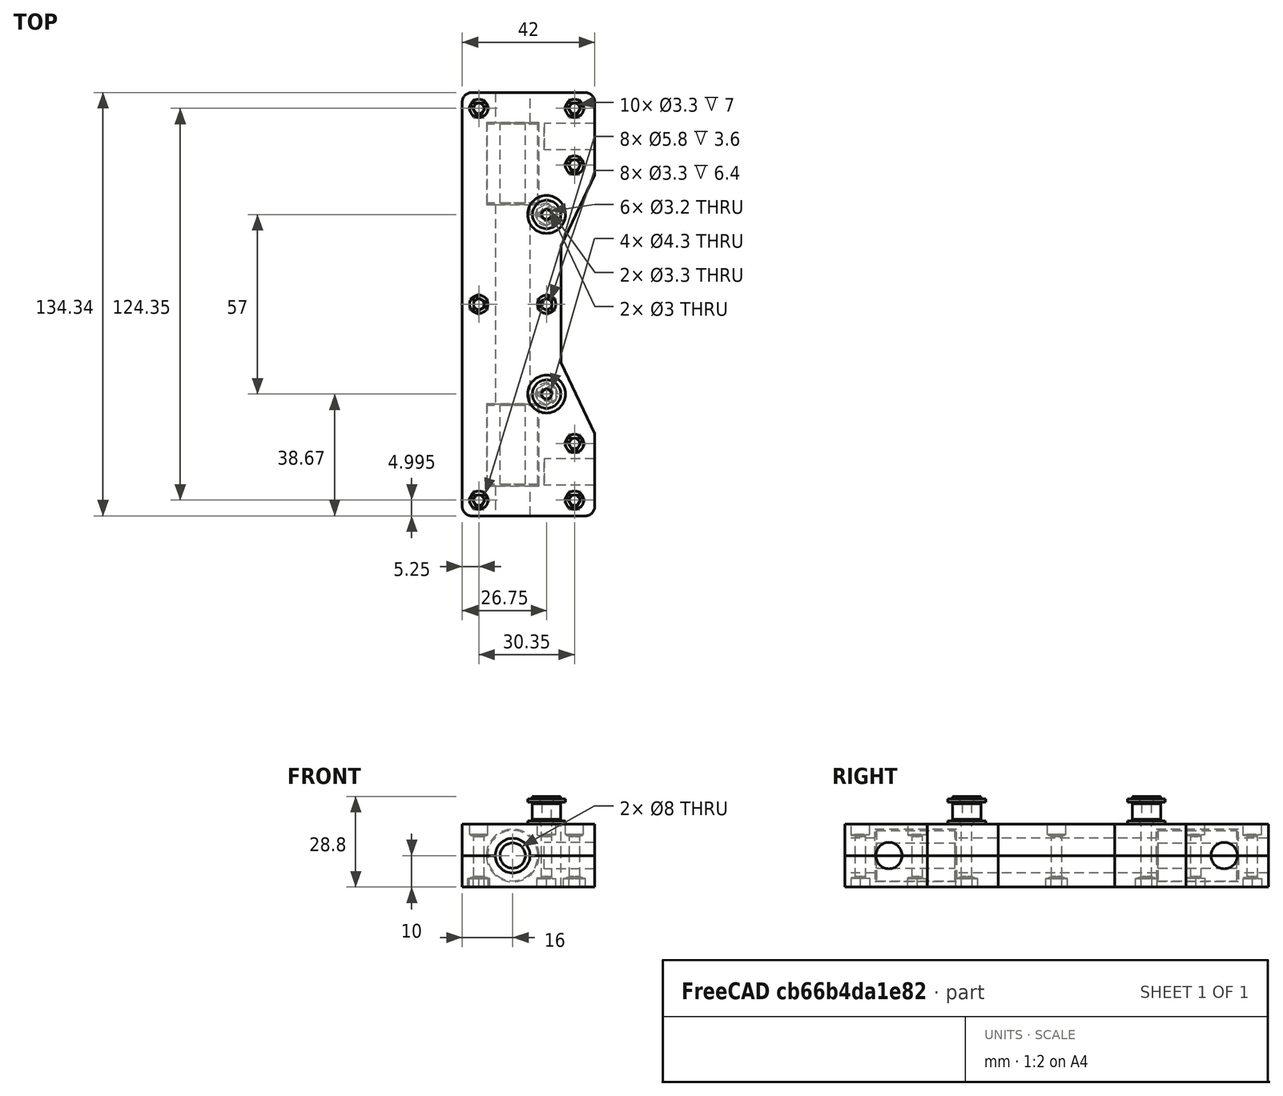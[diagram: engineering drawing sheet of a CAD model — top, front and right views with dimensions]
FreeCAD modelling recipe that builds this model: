
FCSTD DOCUMENT  (FreeCAD 0.16R6706 (Git))
Label: endshaftslid_rodsep_106_35_pullsep_57
License: All rights reserved
LicenseURL: http://en.wikipedia.org/wiki/All_rights_reserved
objects: Part::FeaturePython×11, Part::Prism×10, Part::Cylinder×6, Part::Feature×6, Part::Extrusion×5, Part::Circle×4, Part::MultiFuse×4, Part::Cut×3, Part::Common×3, Part::Box×2, Part::Fillet×2, Part::Compound×2, Part::Polygon×1, Part::Fuse×1
note: 60 computed .brp shape members not serialized (recipe doc carries the construction recipe); baked Part::Feature solids carry a one-line shape summary decoded from their .brp

FEATURE [Part::Box] topsideslid_box
  Height = 10
  Length = 42
  Placement = pos=(-16,-67.175,0) rot=(0,0,1;0rad)
  Width = 134.35
FEATURE [Part::Box] bosidetslid_box
  Height = 10
  Length = 42
  Placement = pos=(-16,-67.175,-10) rot=(0,0,1;0rad)
  Width = 134.35
FEATURE [Part::Fillet] topsideslid_fllt
  Base = -> topsideslid_box
  Edges = 4 edges r=3: [Edge1,Edge3,Edge5,Edge7]
FEATURE [Part::Fillet] botsideslid_fllt
  Base = -> bosidetslid_box
  Edges = 4 edges r=3: [Edge1,Edge3,Edge5,Edge7]
FEATURE [Part::Circle] sliderod_circ
  Angle0 = 0
  Angle1 = 360
  Placement = pos=(0,-68.175,0) rot=(-1,0,0;1.5708rad)
  Radius = 5.5
FEATURE [Part::Extrusion] sliderod
  Base = -> sliderod_circ
  Dir = (0,136.35,0)
  Solid = true
FEATURE [Part::Cylinder] lm8uu_0_ext
  Angle = 360
  Height = 25
  Placement = pos=(0,-57.175,0) rot=(-1,0,0;1.5708rad)
  Radius = 8
FEATURE [Part::Cylinder] lm8uu_0_int
  Angle = 360
  Height = 27
  Placement = pos=(0,-58.175,0) rot=(-1,0,0;1.5708rad)
  Radius = 4
FEATURE [Part::Cut] lm8uu_0
  Base = -> lm8uu_0_ext
  Tool = -> lm8uu_0_int
FEATURE [Part::Circle] lm8uu_0_cont_circ
  Angle0 = 0
  Angle1 = 360
  Placement = pos=(0,-57.675,0) rot=(-1,0,0;1.5708rad)
  Radius = 8.35
FEATURE [Part::Extrusion] lm8uu_0_cont
  Base = -> lm8uu_0_cont_circ
  Dir = (0,26,0)
  Solid = true
FEATURE [Part::FeaturePython] Clone  label="lm8uu_1"  # Draft clone (typed FeaturePython)
  Objects = -> [lm8uu_0]
  Placement = pos=(0,89.35,0) rot=(0,0,1;0rad)
  Scale = (1,1,1)
FEATURE [Part::FeaturePython] Clone001  label="lm8uu_1_cont"  # Draft clone (typed FeaturePython)
  Objects = -> [lm8uu_0_cont]
  Placement = pos=(0,89.35,0) rot=(0,0,1;0rad)
  Scale = (1,1,1)
FEATURE [Part::Circle] holdrod_0_circ
  Angle0 = 0
  Angle1 = 360
  Placement = pos=(10,0,0) rot=(0,1,0;1.5708rad)
  Radius = 4.175
FEATURE [Part::Extrusion] holdrod_0
  Base = -> holdrod_0_circ
  Dir = (17,0,0)
  Placement = pos=(0,-53.175,0) rot=(0,0,1;0rad)
  Solid = true
FEATURE [Part::Circle] holdrod_1_circ
  Angle0 = 0
  Angle1 = 360
  Placement = pos=(10,0,0) rot=(0,1,0;1.5708rad)
  Radius = 4.175
FEATURE [Part::Extrusion] holdrod_1
  Base = -> holdrod_1_circ
  Dir = (17,0,0)
  Placement = pos=(0,53.175,0) rot=(0,0,1;0rad)
  Solid = true
FEATURE [Part::Cylinder] bolt_hole_bolt_shank
  Angle = 360
  Height = 22
  Placement = pos=(0,0,-1) rot=(0,0,1;0rad)
  Radius = 1.65
FEATURE [Part::Cylinder] bolt_hole_bolt_head
  Angle = 360
  Height = 4.3
  Placement = pos=(0,0,16.7) rot=(0,0,1;0rad)
  Radius = 2.9
FEATURE [Part::Prism] bolt_hole_bolt_sup1
  Circumradius = 3.3
  Height = 3.6
  Placement = pos=(0,0,16.4) rot=(0,0,1;0.523599rad)
  Polygon = 3
FEATURE [Part::Cylinder] bolt_hole_bolt_sup1away
  Angle = 360
  Height = 3.6
  Placement = pos=(0,0,16.4) rot=(0,0,1;0rad)
  Radius = 2.9
FEATURE [Part::Common] sup1cut
  Base = -> bolt_hole_bolt_sup1
  Tool = -> bolt_hole_bolt_sup1away
FEATURE [Part::Prism] bolt_hole_bolt_sup2
  Circumradius = 1.8975
  Height = 3.9
  Placement = pos=(0,0,16.1) rot=(0,0,1;0rad)
  Polygon = 6
FEATURE [Part::MultiFuse] bolt_hole_bolt
  Shapes = -> [bolt_hole_bolt_shank,bolt_hole_bolt_head,sup1cut,bolt_hole_bolt_sup2]
FEATURE [Part::Prism] bolt_hole_nut
  Circumradius = 3.455
  Height = 3.7
  Placement = pos=(0,0,-1) rot=(0,0,1;0rad)
  Polygon = 6
FEATURE [Part::Prism] bolt_hole_nutsup1
  Circumradius = 3.3
  Height = 3
  Placement = pos=(0,0,0) rot=(0,0,1;0.523599rad)
  Polygon = 3
FEATURE [Part::Prism] bolt_hole_supnut1away
  Circumradius = 3.455
  Height = 3
  Polygon = 6
FEATURE [Part::Common] supnut1_cut
  Base = -> bolt_hole_nutsup1
  Tool = -> bolt_hole_supnut1away
FEATURE [Part::Prism] bolt_hole_supnut2
  Circumradius = 1.8975
  Height = 3.3
  Polygon = 6
FEATURE [Part::MultiFuse] boltnut
  Placement = pos=(-10.75,0,-10) rot=(0,0,1;1.5708rad)
  Shapes = -> [bolt_hole_bolt,bolt_hole_nut,supnut1_cut,bolt_hole_supnut2]
FEATURE [Part::FeaturePython] Clone002  label="bolt_hole_r"  # Draft clone (typed FeaturePython)
  Objects = -> [boltnut]
  Placement = pos=(10.75,0,-10) rot=(0,0,1;0.523599rad)
  Scale = (1,1,1)
FEATURE [Part::FeaturePython] Clone003  label="bolt_hole_lu"  # Draft clone (typed FeaturePython)
  Objects = -> [boltnut]
  Placement = pos=(-10.75,-62.175,-10) rot=(0,0,1;0rad)
  Scale = (1,1,1)
FEATURE [Part::FeaturePython] Clone004  label="bolt_hole_ld"  # Draft clone (typed FeaturePython)
  Objects = -> [boltnut]
  Placement = pos=(-10.75,62.175,-10) rot=(0,0,1;0rad)
  Scale = (1,1,1)
FEATURE [Part::FeaturePython] Clone005  label="bolt_hole_ru"  # Draft clone (typed FeaturePython)
  Objects = -> [boltnut]
  Placement = pos=(19.6,62.175,-10) rot=(0,0,1;0rad)
  Scale = (1,1,1)
FEATURE [Part::FeaturePython] Clone006  label="bolt_hole_rd"  # Draft clone (typed FeaturePython)
  Objects = -> [boltnut]
  Placement = pos=(19.6,-62.175,-10) rot=(0,0,1;0rad)
  Scale = (1,1,1)
FEATURE [Part::FeaturePython] Clone007  label="bolt_hole_rmu"  # Draft clone (typed FeaturePython)
  Objects = -> [boltnut]
  Placement = pos=(19.6,44.175,-10) rot=(0,0,1;0rad)
  Scale = (1,1,1)
FEATURE [Part::FeaturePython] Clone008  label="bolt_hole_rmd"  # Draft clone (typed FeaturePython)
  Objects = -> [boltnut]
  Placement = pos=(19.6,-44.175,-10) rot=(0,0,1;0rad)
  Scale = (1,1,1)
FEATURE [Part::Cylinder] boltpul_hole_shank
  Angle = 360
  Height = 22
  Placement = pos=(0,0,-1) rot=(0,0,1;0rad)
  Radius = 1.65
FEATURE [Part::Prism] boltpul_hole_head
  Circumradius = 3.455
  Height = 3.7
  Placement = pos=(0,0,-1) rot=(0,0,1;0rad)
  Polygon = 6
FEATURE [Part::Prism] boltpul_hole_sup1
  Circumradius = 3.3
  Height = 3
  Placement = pos=(0,0,0) rot=(0,0,1;0.523599rad)
  Polygon = 3
FEATURE [Part::Prism] boltpul_hole_sup1away
  Circumradius = 3.455
  Height = 3
  Polygon = 6
FEATURE [Part::Common] sup1cut001
  Base = -> boltpul_hole_sup1
  Tool = -> boltpul_hole_sup1away
FEATURE [Part::Prism] boltpul_hole_sup2
  Circumradius = 1.8975
  Height = 3.3
  Polygon = 6
FEATURE [Part::MultiFuse] boltpul_hole
  Placement = pos=(10.75,28.5,-10) rot=(0,0,1;0.523599rad)
  Shapes = -> [boltpul_hole_shank,boltpul_hole_head,sup1cut001,boltpul_hole_sup2]
FEATURE [Part::Feature] idlepull_01
  shape: bbox 12 x 12 x 1 mm, 4 faces (baked)
FEATURE [Part::Feature] idlepull_02
  shape: bbox 7 x 7 x 0.5 mm, 4 faces (baked)
FEATURE [Part::Feature] idlepull_03
  shape: bbox 9 x 9 x 5 mm, 4 faces (baked)
FEATURE [Part::Feature] idlepull_04
  shape: bbox 7 x 7 x 0.5 mm, 4 faces (baked)
FEATURE [Part::Feature] idlepull_05
  shape: bbox 12 x 12 x 1 mm, 4 faces (baked)
FEATURE [Part::Feature] idlepull_06
  shape: bbox 9 x 9 x 0.8 mm, 4 faces (baked)
FEATURE [Part::Compound] idlepull_0
  Links = -> [idlepull_01,idlepull_02,idlepull_03,idlepull_04,idlepull_05,idlepull_06]
FEATURE [Part::FeaturePython] Clone009  label="boltpul_hole_1"  # Draft clone (typed FeaturePython)
  Objects = -> [boltpul_hole]
  Placement = pos=(10.75,-28.5,-10) rot=(0,0,1;0.523599rad)
  Scale = (1,1,1)
FEATURE [Part::FeaturePython] Clone010  label="idlepull_1"  # Draft clone (typed FeaturePython)
  Objects = -> [idlepull_0]
  Placement = pos=(0,-57,0) rot=(0,0,1;0rad)
  Scale = (1,1,1)
FEATURE [Part::Compound] idlepulls
  Links = -> [idlepull_0,Clone010]
FEATURE [Part::Polygon] dent_plane
  Close = true
  Nodes = (4) [(27,43.175,-11),(15.35,18.5,-11),(15.35,-18.5,-11),(27,-43.175,-11)]
FEATURE [Part::Extrusion] dent
  Base = -> dent_plane
  Dir = (0,0,22)
  Solid = true
FEATURE [Part::MultiFuse] holes
  Shapes = -> [sliderod,lm8uu_0_cont,Clone001,holdrod_0,holdrod_1,boltnut,Clone002,Clone003,Clone004,Clone005,Clone006,Clone007,Clone008,boltpul_hole,Clone009,dent]
FEATURE [Part::Fuse] yslider_nx_bear
  Base = -> lm8uu_0
  Tool = -> Clone
FEATURE [Part::Cut] yslider_nx_top
  Base = -> topsideslid_fllt
  Tool = -> holes
FEATURE [Part::Cut] yslider_nx_bot
  Base = -> botsideslid_fllt
  Tool = -> holes
